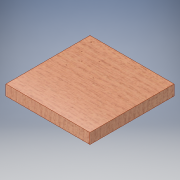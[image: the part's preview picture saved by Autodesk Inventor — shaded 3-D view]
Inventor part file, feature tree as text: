
AUTODESK INVENTOR PART (.ipt)
format: ipt  version: 2017 (Build 210142000, 142)  size: 110,592 bytes
history: native  units: in
note: dims shown in document units (in); Inventor stores cm internally (conversion verified against a paired STEP export)
features: extrude x1, sketch x1
ambient origin geometry x8: Origin, YZ Plane, XZ Plane, XY Plane, X Axis, Y Axis, Z Axis, Center Point
bodies: Solid1 (feature_tree)
feature tree (2):
  extrude  "Extrusion1"  Depth=6.0in
  sketch  "Sketch1"  dims[d0=6.0in d1=6.0in d2=0.75in d3=0.0in]
